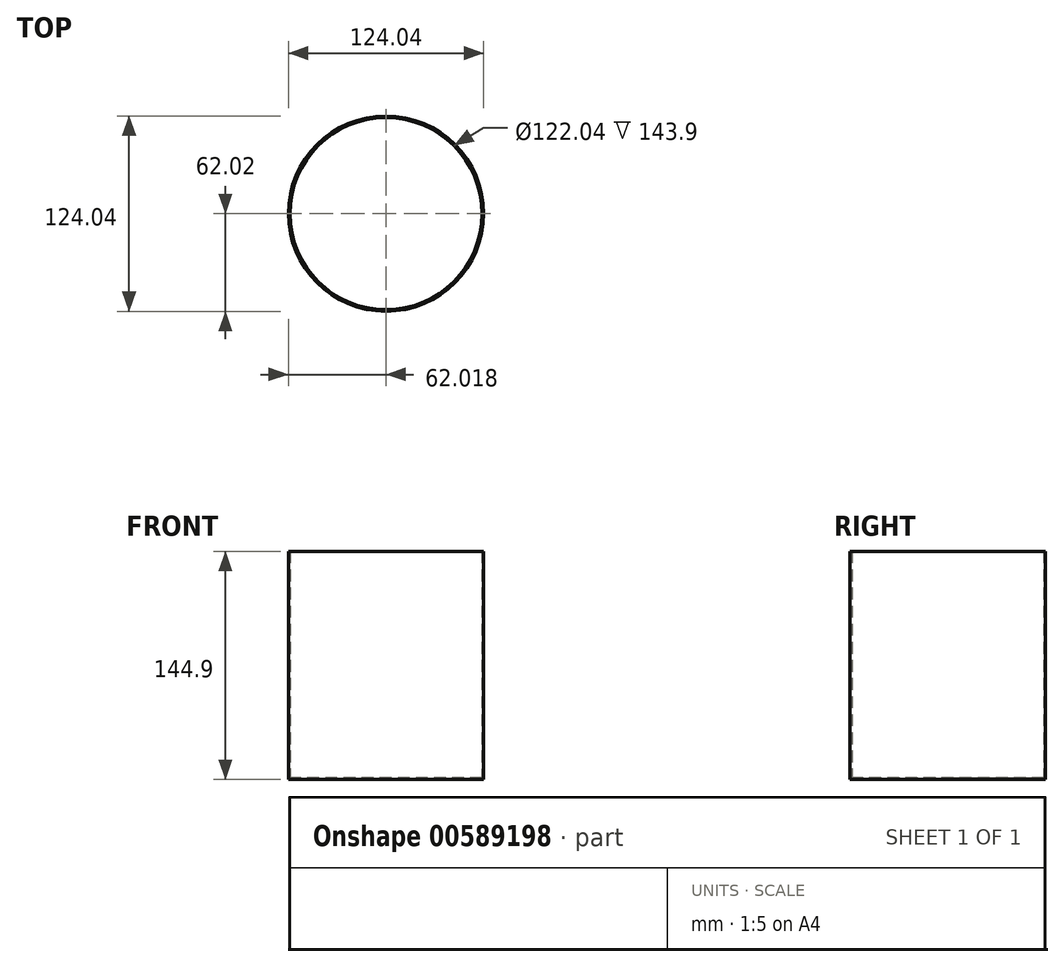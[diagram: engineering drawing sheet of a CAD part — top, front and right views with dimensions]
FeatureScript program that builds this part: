
annotation { "Feature Type Name" : "Feature", "Feature Type Description" : "" }
export const myFeature = defineFeature(function(context is Context, id is Id, definition is map)
    precondition{}
    {
        {
            var Q0;
            Q0=qCreatedBy(makeId("Top.planeOp"),FACE);
            var sketch = newSketch(context, id + "F0", { "sketchPlane" : qUnion([Q0])});
            skCircle(sketch, "E0", {"center": v(3.5, 0) * mm, "radius": 62.02 * mm});
            skSolve(sketch);
        }
        {
            var Q0;
            Q0=makeQuery(id+"F0.imprint","IMPRINT",FACE,{"disambiguationData":[TD([[makeQuery(id+"F0.imprint","IMPRINT",EDGE,{"derivedFrom":sQuery(id+"F0.wireOp",EDGE,"E0")}),1.0]])]});
            extrude(context, id + "F1", {"entities" : qUnion([Q0]), "depth" : 144.9 * mm, "offsetDistance" : 25 * mm});
        }
        {
            var Q0;
            Q0=makeQuery(id+"F1.opExtrude","CAP_FACE",FACE,{"disambiguationData":[OSD([sQuery(id+"F0.wireOp",EDGE,"E0")])],"isStart":false});
            shell(context, id + "F2", {"entities" : qUnion([Q0]), "thickness" : 1 * mm});
        }
        {
            var Q0;
            Q0=qCreatedBy(makeId("Front.planeOp"),FACE);
            var sketch = newSketch(context, id + "F3", { "sketchPlane" : qUnion([Q0])});
            skFitSpline(sketch, "E1", {"points": [v(56.01, 106.6) * mm, v(101.12, 93.19) * mm, v(56.97, 17.53) * mm], "startDerivative": vector(145.37, -10.67) * mm, "endDerivative": vector(-129.34, -159.8) * mm});
            skSolve(sketch);
        }
    });
